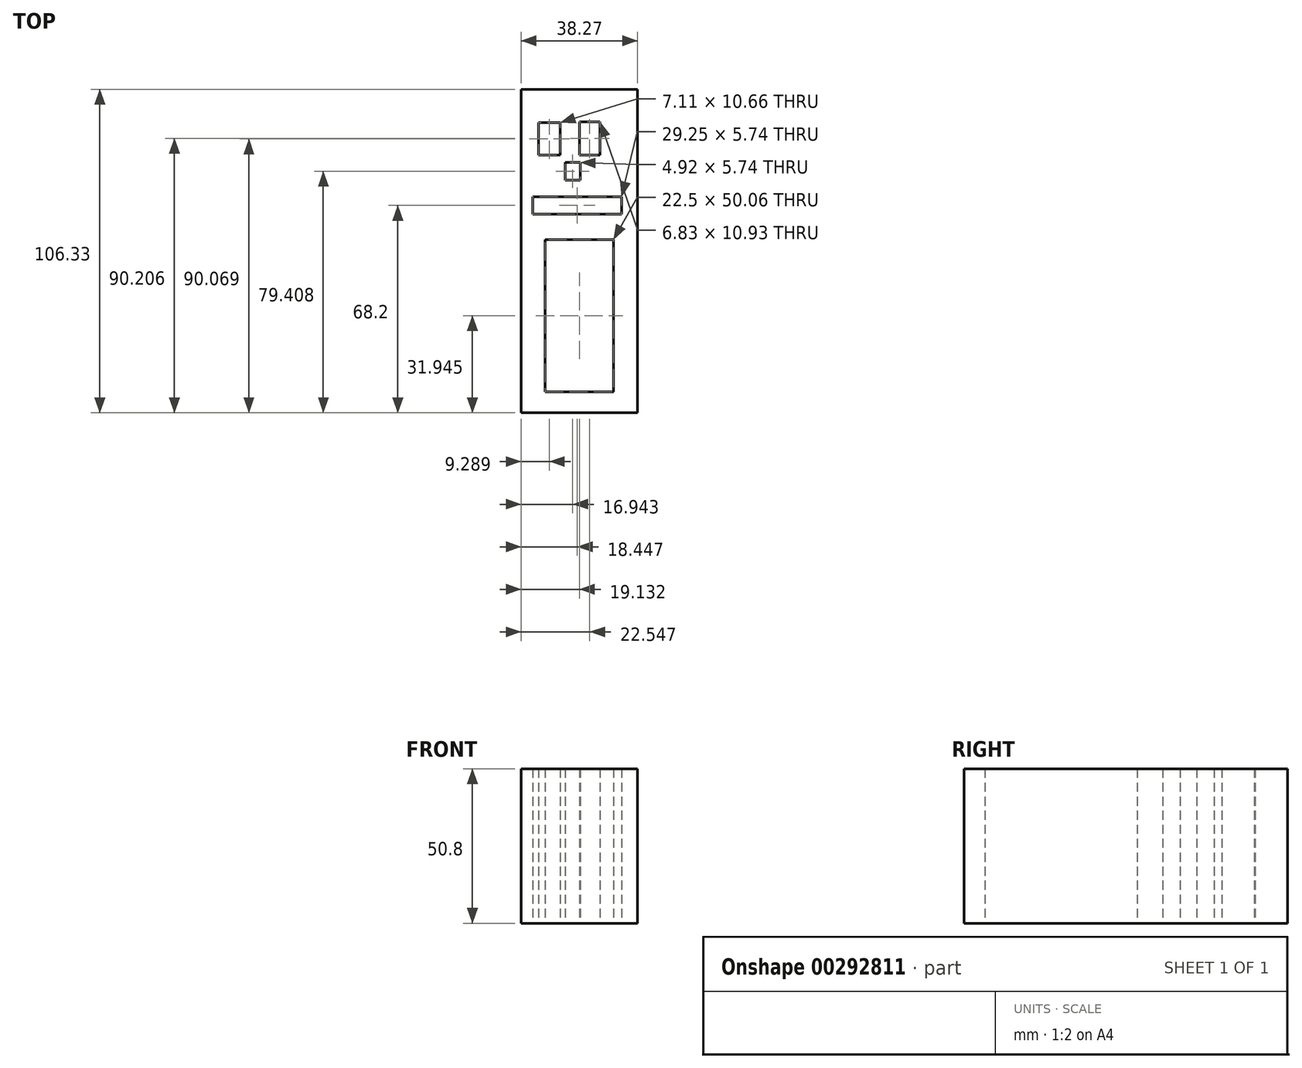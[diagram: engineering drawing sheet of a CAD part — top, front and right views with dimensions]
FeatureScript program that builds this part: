
annotation { "Feature Type Name" : "Feature", "Feature Type Description" : "" }
export const myFeature = defineFeature(function(context is Context, id is Id, definition is map)
    precondition{}
    {
        {
            var Q0;
            Q0=qCreatedBy(makeId("Top.planeOp"),FACE);
            var sketch = newSketch(context, id + "F0", { "sketchPlane" : qUnion([Q0])});
            skLineSegment(sketch, "E0.bottom", {"start": v(-59.91, 52.6) * mm, "end": v(-21.64, 52.6) * mm});
            skLineSegment(sketch, "E0.left", {"start": v(-59.91, 52.6) * mm, "end": v(-59.91, 6.67) * mm});
            skLineSegment(sketch, "E0.right", {"start": v(-21.64, 52.6) * mm, "end": v(-21.64, 6.67) * mm});
            skLineSegment(sketch, "E1.left", {"start": v(-59.91, 39.47) * mm, "end": v(-59.91, 34.83) * mm});
            skLineSegment(sketch, "E1.right", {"start": v(-21.64, 39.47) * mm, "end": v(-21.64, 34.83) * mm});
            skLineSegment(sketch, "E2.bottom", {"start": v(-54.17, 41.66) * mm, "end": v(-47.07, 41.66) * mm});
            skLineSegment(sketch, "E2.top", {"start": v(-54.17, 31) * mm, "end": v(-47.07, 31) * mm});
            skLineSegment(sketch, "E2.left", {"start": v(-54.17, 41.66) * mm, "end": v(-54.17, 31) * mm});
            skLineSegment(sketch, "E2.right", {"start": v(-47.07, 41.66) * mm, "end": v(-47.07, 31) * mm});
            skPoint(sketch, "E3.firstSnap0", {"position": v(-40.78, 39.47) * mm});
            skLineSegment(sketch, "E3.bottom", {"start": v(-40.78, 41.93) * mm, "end": v(-33.95, 41.93) * mm});
            skLineSegment(sketch, "E3.top", {"start": v(-40.78, 31) * mm, "end": v(-33.95, 31) * mm});
            skLineSegment(sketch, "E3.left", {"start": v(-40.78, 41.93) * mm, "end": v(-40.78, 31) * mm});
            skLineSegment(sketch, "E3.right", {"start": v(-33.95, 41.93) * mm, "end": v(-33.95, 31) * mm});
            skLineSegment(sketch, "E4.bottom", {"start": v(-45.43, 28.54) * mm, "end": v(-40.5, 28.54) * mm});
            skLineSegment(sketch, "E4.top", {"start": v(-45.43, 22.8) * mm, "end": v(-40.5, 22.8) * mm});
            skLineSegment(sketch, "E4.left", {"start": v(-45.43, 28.54) * mm, "end": v(-45.43, 22.8) * mm});
            skLineSegment(sketch, "E4.right", {"start": v(-40.5, 28.54) * mm, "end": v(-40.5, 22.8) * mm});
            skLineSegment(sketch, "E5.bottom", {"start": v(-56.09, 17.33) * mm, "end": v(-26.84, 17.33) * mm});
            skLineSegment(sketch, "E5.top", {"start": v(-56.09, 11.6) * mm, "end": v(-26.84, 11.6) * mm});
            skLineSegment(sketch, "E5.left", {"start": v(-56.09, 17.33) * mm, "end": v(-56.09, 11.6) * mm});
            skLineSegment(sketch, "E5.right", {"start": v(-26.84, 17.33) * mm, "end": v(-26.84, 11.6) * mm});
            skPoint(sketch, "E6.startSnap0", {"position": v(-56.09, 14.46) * mm});
            skLineSegment(sketch, "E7", {"start": v(-40.5, 22.8) * mm, "end": v(-40.6, 28.54) * mm});
            skLineSegment(sketch, "E8", {"start": v(-59.91, 6.67) * mm, "end": v(-59.91, -53.74) * mm});
            skLineSegment(sketch, "E9", {"start": v(-21.64, 6.67) * mm, "end": v(-21.64, -53.74) * mm});
            skLineSegment(sketch, "E10", {"start": v(-59.91, -53.74) * mm, "end": v(-21.64, -53.74) * mm});
            skLineSegment(sketch, "E11.trimOffspring", {"start": v(-56.09, -53.74) * mm, "end": v(-56.09, -54.29) * mm});
            skLineSegment(sketch, "E12.trimOffspring", {"start": v(-26.57, -53.74) * mm, "end": v(-26.57, -54.29) * mm});
            skLineSegment(sketch, "E13.trimOffspring", {"start": v(-40.64, 31) * mm, "end": v(-40.78, 39.47) * mm});
            skPoint(sketch, "E14.start.orphan", {"position": v(-40.78, 52.6) * mm});
            skLineSegment(sketch, "E15.bottom", {"start": v(-52.03, 3.23) * mm, "end": v(-29.53, 3.23) * mm});
            skLineSegment(sketch, "E15.top", {"start": v(-52.03, -46.82) * mm, "end": v(-29.53, -46.82) * mm});
            skLineSegment(sketch, "E15.left", {"start": v(-52.03, 3.23) * mm, "end": v(-52.03, -46.82) * mm});
            skLineSegment(sketch, "E15.right", {"start": v(-29.53, 3.23) * mm, "end": v(-29.53, -46.82) * mm});
            skSolve(sketch);
        }
        {
            var Q0;
            {var subQ13=sQuery(id+"F0.wireOp",EDGE,"E0.bottom");Q0=makeQuery(id+"F0.imprint","IMPRINT",FACE,{"disambiguationData":[TD([[makeQuery(id+"F0.imprint","IMPRINT",EDGE,{"derivedFrom":subQ13}),-1.0]])]});}
            extrude(context, id + "F1", {"entities" : qUnion([Q0]), "depth" : 50.8 * mm});
        }
    });
